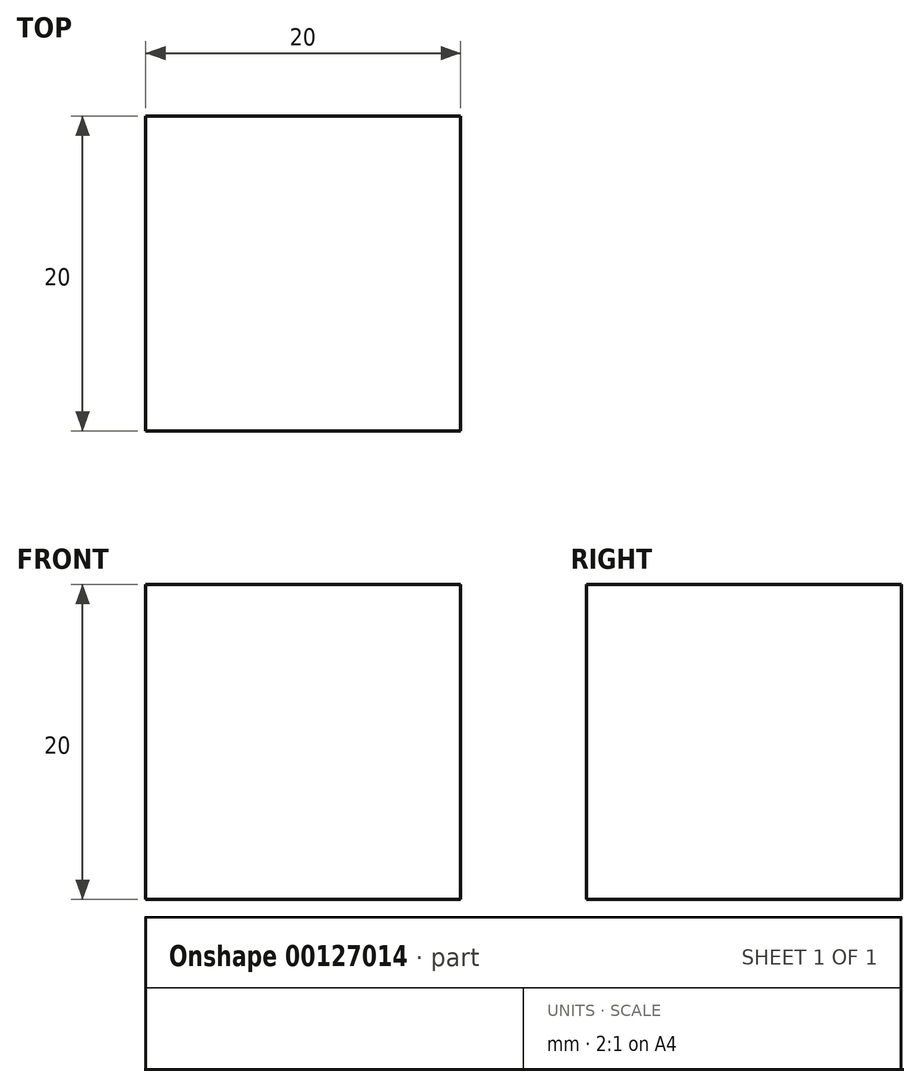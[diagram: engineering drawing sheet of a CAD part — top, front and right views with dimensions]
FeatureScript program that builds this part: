
annotation { "Feature Type Name" : "Feature", "Feature Type Description" : "" }
export const myFeature = defineFeature(function(context is Context, id is Id, definition is map)
    precondition{}
    {
        {
            var Q0;
            Q0=qCreatedBy(makeId("Top.planeOp"),FACE);
            var sketch = newSketch(context, id + "F0", { "sketchPlane" : qUnion([Q0])});
            skLineSegment(sketch, "E0.bottom", {"start": v(10, -10) * mm, "end": v(-10, -10) * mm});
            skLineSegment(sketch, "E0.top", {"start": v(10, 10) * mm, "end": v(-10, 10) * mm});
            skLineSegment(sketch, "E0.left", {"start": v(10, -10) * mm, "end": v(10, 10) * mm});
            skLineSegment(sketch, "E0.right", {"start": v(-10, -10) * mm, "end": v(-10, 10) * mm});
            skPoint(sketch, "E0.middle", {"position": v(0, 0) * mm});
            skSolve(sketch);
        }
        {
            var Q0;
            Q0=makeQuery(id+"F0.imprint","IMPRINT",FACE,{"disambiguationData":[TD([[makeQuery(id+"F0.imprint","IMPRINT",EDGE,{"derivedFrom":sQuery(id+"F0.wireOp",EDGE,"E0.bottom")}),-1.0]])]});
            extrude(context, id + "F1", {"entities" : qUnion([Q0]), "endBound" : BoundingType.SYMMETRIC, "depth" : 20 * mm});
        }
    });
